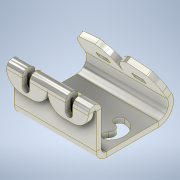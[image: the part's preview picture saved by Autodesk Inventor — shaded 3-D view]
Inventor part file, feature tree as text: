
AUTODESK INVENTOR PART (.ipt)
format: ipt  version: 2021 (Build 250183000, 183)  size: 422,400 bytes
history: native  units: in
note: dims shown in document units (in); Inventor stores cm internally (conversion verified against a paired STEP export)
features: sheet_metal_op x10, other x8, sketch x7, chamfer x2, mirror x1
ambient origin geometry x8: Origin, YZ Plane, XZ Plane, XY Plane, X Axis, Y Axis, Z Axis, Center Point
bodies: Solid1 (feature_tree)
feature tree (28):
  sheet_metal_op  "Face1"
  sheet_metal_op  "Flange1"
  sheet_metal_op  "Flange2"
  sheet_metal_op  "Hem1"
  sheet_metal_op  "Unfold1"
  sheet_metal_op  "Refold1"
  chamfer  "Corner Round1"
  chamfer  "Corner Round2"
  other  "Corner Chamfer1"
  mirror  "Mirror1"
  sketch  "Sketch1"  dims[d0=0.05in]
  other  "Plate1"
  sketch  "Sketch2"  dims[d1=0.05in]
  other  "Plate2"
  sheet_metal_op  "Bend1"
  sheet_metal_op  "Corner1"
  sketch  "Sketch3"  dims[d2=0.025in]
  other  "Plate3"
  sheet_metal_op  "Bend2"
  sheet_metal_op  "Corner2"
  sketch  "Sketch5"  dims[d4=0.05in]
  sketch  "Sketch6"  dims[d5=0.5in d6=90.0deg d7=0.05in]
  sketch  "Sketch7"  dims[d8=0.2in d9=0.05in d10=0.05in d11=0.05in d12=0.025in d13=0.1in d14=0.05in d15=0.5in d16=120.0deg d17=0.1in d18=0.0in d19=0.2in d20=0.05in d21=0.05in d22=0.05in d23=0.025in d24=0.1in d25=0.05in d26=0.2in d27=0.025in d28=0.0125in d29=0.05in d30=0.0in d31=0.05in d32=0.0in d33=0.05in d34=0.0in d35=0.25in d36=0.15in d37=0.1in d38=0.25in d39=45.0deg]
  other  "Cut1"
  other  "Cut2"
  other  "Cut3"
  sketch  "Sketch4"  dims[d3=0.1in]
  other  "Definition1"
